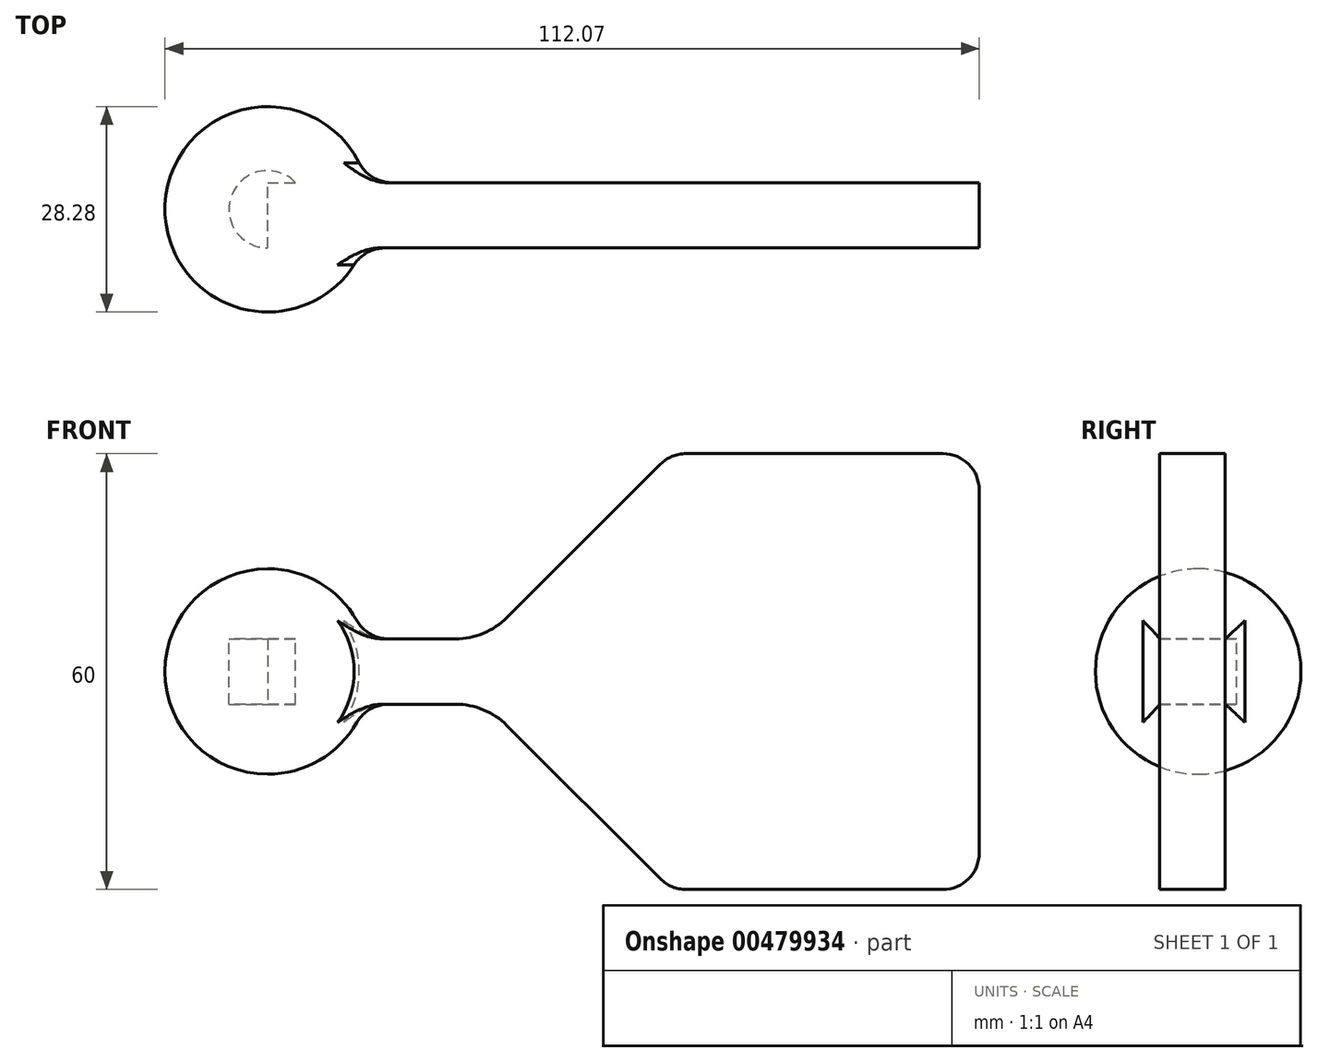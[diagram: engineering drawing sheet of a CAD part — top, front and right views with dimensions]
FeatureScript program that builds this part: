
annotation { "Feature Type Name" : "Feature", "Feature Type Description" : "" }
export const myFeature = defineFeature(function(context is Context, id is Id, definition is map)
    precondition{}
    {
        {
            var Q0;
            Q0=qCreatedBy(makeId("Front.planeOp"),FACE);
            var sketch = newSketch(context, id + "F0", { "sketchPlane" : qUnion([Q0])});
            skLineSegment(sketch, "E0.bottom", {"start": v(35, 30) * mm, "end": v(-7.43, 30) * mm});
            skLineSegment(sketch, "E0.top", {"start": v(35, -30) * mm, "end": v(-7.43, -30) * mm});
            skLineSegment(sketch, "E0.left", {"start": v(35, 30) * mm, "end": v(35, -30) * mm});
            skPoint(sketch, "E0.middle", {"position": v(0, 0) * mm});
            skLineSegment(sketch, "E1.bottom", {"start": v(-62.93, 4.5) * mm, "end": v(-37.07, 4.5) * mm});
            skLineSegment(sketch, "E1.top", {"start": v(-62.93, -4.5) * mm, "end": v(-37.07, -4.5) * mm});
            skLineSegment(sketch, "E2", {"start": v(-62.93, 4.5) * mm, "end": v(-62.93, -4.5) * mm});
            skLineSegment(sketch, "E3", {"start": v(-30, 7.43) * mm, "end": v(-7.43, 30) * mm});
            skLineSegment(sketch, "E4.MirrorCS", {"start": v(-30, -7.43) * mm, "end": v(-7.43, -30) * mm});
            skPoint(sketch, "E5.visualSharp", {"position": v(-32.93, 4.5) * mm});
            skArc(sketch, "E5.filletArc", {"start": v(-37.07, 4.5) * mm, "mid": v(-33.24, 5.26) * mm, "end": v(-30, 7.43) * mm});
            skPoint(sketch, "E6.newPointA", {"position": v(-32.93, -4.5) * mm});
            skArc(sketch, "E6.filletArc", {"start": v(-30, -7.43) * mm, "mid": v(-33.24, -5.26) * mm, "end": v(-37.07, -4.5) * mm});
            skSolve(sketch);
        }
        {
            var Q0;
            Q0=makeQuery(id+"F0.imprint","IMPRINT",FACE,{"disambiguationData":[TD([[makeQuery(id+"F0.imprint","IMPRINT",EDGE,{"derivedFrom":sQuery(id+"F0.wireOp",EDGE,"E0.bottom")}),1.0]])]});
            extrude(context, id + "F1", {"entities" : qUnion([Q0]), "depth" : 9 * mm});
        }
        {
            var Q0;
            Q0=makeQuery(id+"F1.opExtrude","SWEPT_FACE",FACE,{"disambiguationData":[OSD([sQuery(id+"F0.wireOp",EDGE,"E2")])]});
            var sketch = newSketch(context, id + "F2", { "sketchPlane" : qUnion([Q0])});
            skArc(sketch, "E7", {"start": v(3.68, -14.14) * mm, "mid": v(17.82, 0) * mm, "end": v(3.68, 14.14) * mm});
            skLineSegment(sketch, "E8", {"start": v(3.68, 14.14) * mm, "end": v(3.68, -14.14) * mm});
            skSolve(sketch);
        }
        {
            var Q0;
            {var subQ1=sQuery(id+"F2.wireOp",EDGE,"E7");Q0=makeQuery(id+"F2.imprint","IMPRINT",FACE,{"disambiguationData":[TD([[makeQuery(id+"F2.imprint","IMPRINT",EDGE,{"derivedFrom":subQ1}),1.0]])]});}
            var Q1;
            Q1=sQuery(id+"F2.wireOp",EDGE,"E8");
            revolve(context, id + "F3", {"operationType" : NewBodyOperationType.ADD, "entities" : qUnion([Q0]), "axis" : qUnion([Q1]), "revolveType" : RevolveType.FULL});
        }
        {
            var Q0;
            Q0=makeQuery(id+"F3.boolean.opBoolean","INTERSECT",EDGE,{"derivedFrom":[makeQuery(id+"F1.opExtrude","SWEPT_FACE",FACE,{"disambiguationData":[OSD([sQuery(id+"F0.wireOp",EDGE,"E1.bottom")])]}),makeQuery(id+"F3.opRevolve","SWEPT_FACE",FACE,{"disambiguationData":[OSD([sQuery(id+"F2.wireOp",EDGE,"E7")])]})]});
            var Q1;
            Q1=makeQuery(id+"F3.boolean.opBoolean","INTERSECT",EDGE,{"derivedFrom":[makeQuery(id+"F1.opExtrude","CAP_FACE",FACE,{"disambiguationData":[OSD([sQuery(id+"F0.wireOp",EDGE,"E0.bottom"),sQuery(id+"F0.wireOp",EDGE,"E0.top"),sQuery(id+"F0.wireOp",EDGE,"E0.left"),sQuery(id+"F0.wireOp",EDGE,"E1.bottom"),sQuery(id+"F0.wireOp",EDGE,"E1.top"),sQuery(id+"F0.wireOp",EDGE,"E2"),sQuery(id+"F0.wireOp",EDGE,"E3"),sQuery(id+"F0.wireOp",EDGE,"E4.MirrorCS"),sQuery(id+"F0.wireOp",EDGE,"E5.filletArc"),sQuery(id+"F0.wireOp",EDGE,"E6.filletArc")])],"isStart":true}),makeQuery(id+"F3.opRevolve","SWEPT_FACE",FACE,{"disambiguationData":[OSD([sQuery(id+"F2.wireOp",EDGE,"E7")])]})]});
            var Q2;
            Q2=makeQuery(id+"F3.boolean.opBoolean","INTERSECT",EDGE,{"derivedFrom":[makeQuery(id+"F1.opExtrude","SWEPT_FACE",FACE,{"disambiguationData":[OSD([sQuery(id+"F0.wireOp",EDGE,"E1.top")])]}),makeQuery(id+"F3.opRevolve","SWEPT_FACE",FACE,{"disambiguationData":[OSD([sQuery(id+"F2.wireOp",EDGE,"E7")])]})]});
            var Q3;
            Q3=makeQuery(id+"F3.boolean.opBoolean","INTERSECT",EDGE,{"derivedFrom":[makeQuery(id+"F1.opExtrude","CAP_FACE",FACE,{"disambiguationData":[OSD([sQuery(id+"F0.wireOp",EDGE,"E0.bottom"),sQuery(id+"F0.wireOp",EDGE,"E0.top"),sQuery(id+"F0.wireOp",EDGE,"E0.left"),sQuery(id+"F0.wireOp",EDGE,"E1.bottom"),sQuery(id+"F0.wireOp",EDGE,"E1.top"),sQuery(id+"F0.wireOp",EDGE,"E2"),sQuery(id+"F0.wireOp",EDGE,"E3"),sQuery(id+"F0.wireOp",EDGE,"E4.MirrorCS"),sQuery(id+"F0.wireOp",EDGE,"E5.filletArc"),sQuery(id+"F0.wireOp",EDGE,"E6.filletArc")])],"isStart":false}),makeQuery(id+"F3.opRevolve","SWEPT_FACE",FACE,{"disambiguationData":[OSD([sQuery(id+"F2.wireOp",EDGE,"E7")])]})]});
            fillet(context, id + "F4", {"entities" : qUnion([Q0, Q1, Q2, Q3]), "radius" : 5 * mm, "tangentPropagation" : true, "allowEdgeOverflow" : false});
        }
        {
            var Q0;
            Q0=makeQuery(id+"F1.opExtrude","SWEPT_EDGE",EDGE,{"disambiguationData":[OSD([sQuery(id+"F0.wireOp",EDGE,"E0.top"),sQuery(id+"F0.wireOp",EDGE,"E0.left")])]});
            var Q1;
            Q1=makeQuery(id+"F1.opExtrude","SWEPT_EDGE",EDGE,{"disambiguationData":[OSD([sQuery(id+"F0.wireOp",EDGE,"E0.bottom"),sQuery(id+"F0.wireOp",EDGE,"E0.left")])]});
            var Q2;
            Q2=makeQuery(id+"F1.opExtrude","SWEPT_EDGE",EDGE,{"disambiguationData":[OSD([sQuery(id+"F0.wireOp",EDGE,"E0.bottom"),sQuery(id+"F0.wireOp",EDGE,"E3")])]});
            var Q3;
            Q3=makeQuery(id+"F1.opExtrude","SWEPT_EDGE",EDGE,{"disambiguationData":[OSD([sQuery(id+"F0.wireOp",EDGE,"E0.top"),sQuery(id+"F0.wireOp",EDGE,"E4.MirrorCS")])]});
            fillet(context, id + "F5", {"entities" : qUnion([Q0, Q1, Q2, Q3]), "radius" : 5 * mm, "tangentPropagation" : true, "allowEdgeOverflow" : false});
        }
    });
